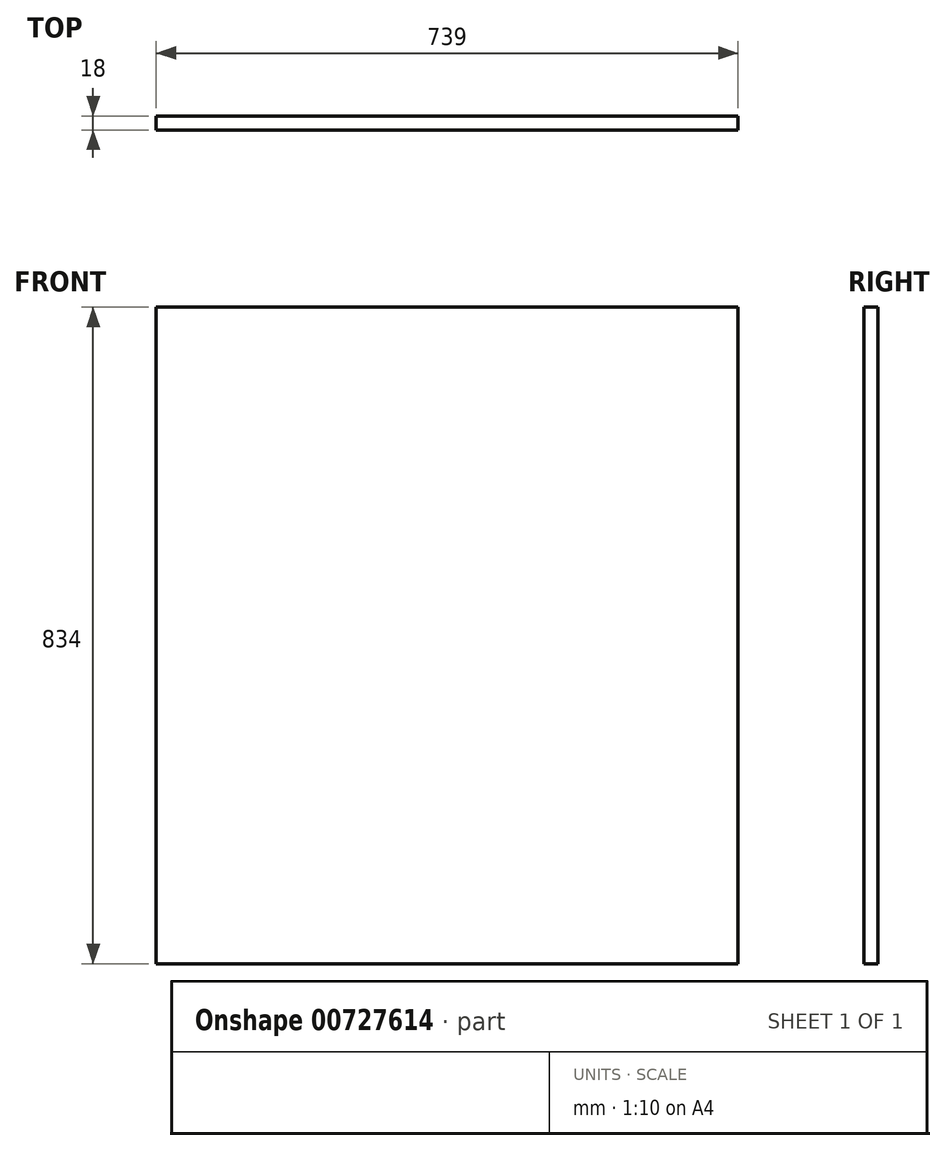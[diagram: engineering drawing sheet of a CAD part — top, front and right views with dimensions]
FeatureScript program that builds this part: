
annotation { "Feature Type Name" : "Feature", "Feature Type Description" : "" }
export const myFeature = defineFeature(function(context is Context, id is Id, definition is map)
    precondition{}
    {
        {
            var Q0;
            Q0=qCreatedBy(makeId("Front.planeOp"),FACE);
            var sketch = newSketch(context, id + "F0", { "sketchPlane" : qUnion([Q0])});
            skLineSegment(sketch, "E0.bottom", {"start": v(-369.5, -417) * mm, "end": v(369.5, -417) * mm});
            skLineSegment(sketch, "E0.top", {"start": v(-369.5, 417) * mm, "end": v(369.5, 417) * mm});
            skLineSegment(sketch, "E0.left", {"start": v(-369.5, -417) * mm, "end": v(-369.5, 417) * mm});
            skLineSegment(sketch, "E0.right", {"start": v(369.5, -417) * mm, "end": v(369.5, 417) * mm});
            skPoint(sketch, "E0.middle", {"position": v(0, 0) * mm});
            skSolve(sketch);
        }
        {
            var Q0;
            Q0 = qSketchRegion(id + "F0", true);
            extrude(context, id + "F1", {"entities" : qUnion([Q0]), "depth" : 18 * mm, "offsetDistance" : 25 * mm});
        }
    });
